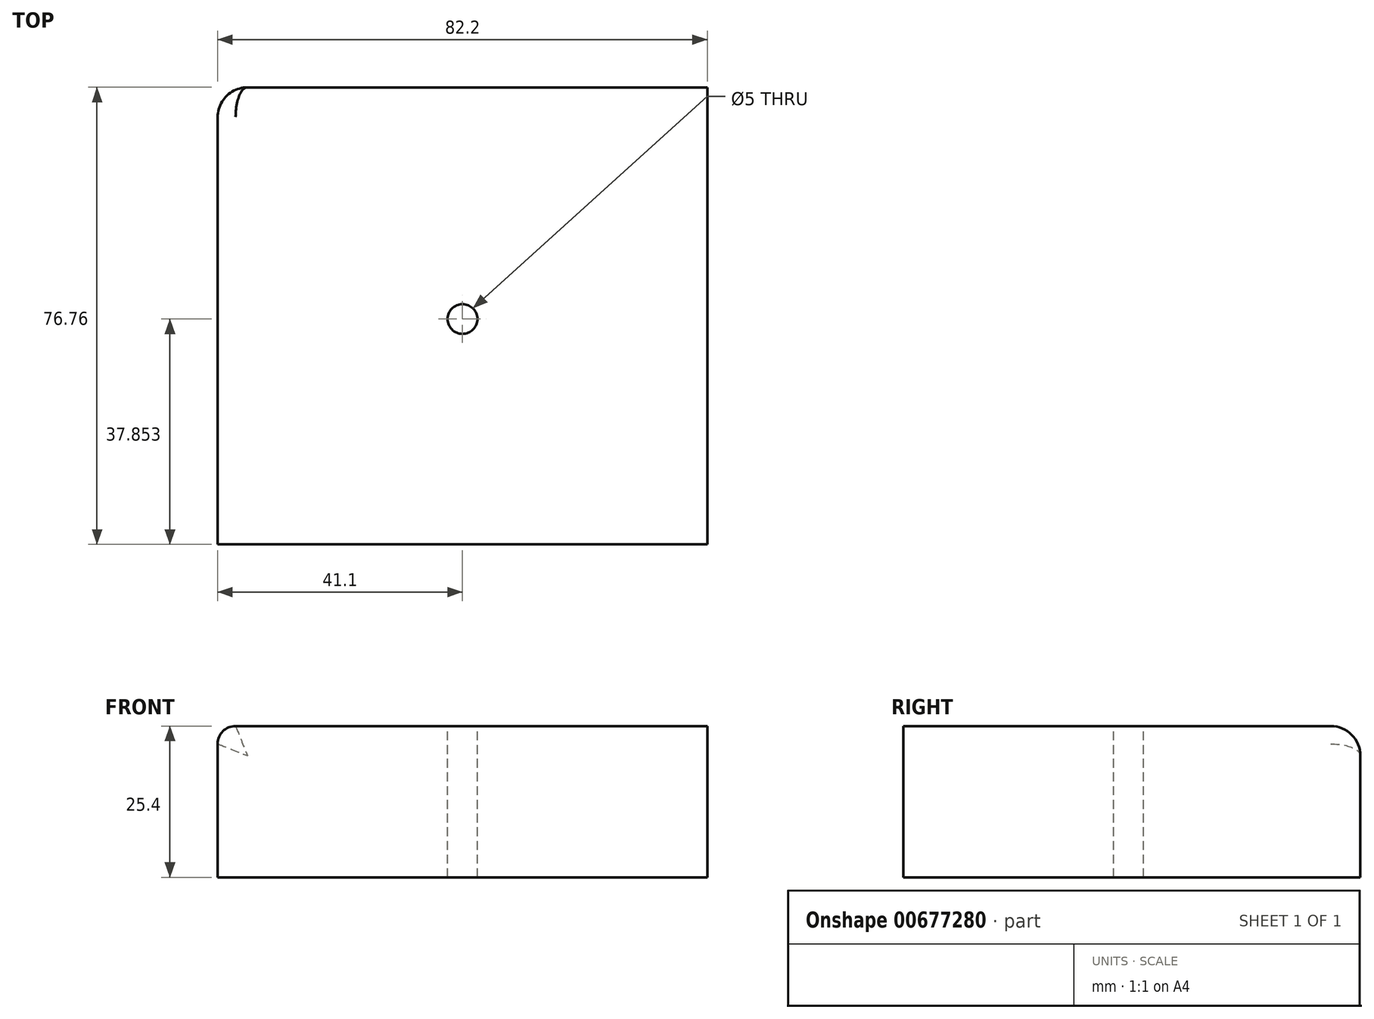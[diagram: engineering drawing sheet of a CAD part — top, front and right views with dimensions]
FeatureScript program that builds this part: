
annotation { "Feature Type Name" : "Feature", "Feature Type Description" : "" }
export const myFeature = defineFeature(function(context is Context, id is Id, definition is map)
    precondition{}
    {
        {
            var Q0;
            Q0=qCreatedBy(makeId("Top.planeOp"),FACE);
            var sketch = newSketch(context, id + "F0", { "sketchPlane" : qUnion([Q0])});
            skLineSegment(sketch, "E0.bottom", {"start": v(41.1, 38.38) * mm, "end": v(-41.1, 38.38) * mm});
            skLineSegment(sketch, "E0.top", {"start": v(41.1, -38.38) * mm, "end": v(-41.1, -38.38) * mm});
            skLineSegment(sketch, "E0.left", {"start": v(41.1, 38.38) * mm, "end": v(41.1, -38.38) * mm});
            skLineSegment(sketch, "E0.right", {"start": v(-41.1, 38.38) * mm, "end": v(-41.1, -38.38) * mm});
            skPoint(sketch, "E0.middle", {"position": v(0, 0) * mm});
            skSolve(sketch);
        }
        {
            var Q0;
            Q0 = qSketchRegion(id + "F0", true);
            extrude(context, id + "F1", {"entities" : qUnion([Q0]), "depth" : 25.4 * mm, "offsetDistance" : 25.4 * mm});
        }
        {
            var Q0;
            Q0=makeQuery(id+"F1.opExtrude","CAP_EDGE",EDGE,{"disambiguationData":[OSD([sQuery(id+"F0.wireOp",EDGE,"E0.right")])],"isStart":false});
            fillet(context, id + "F2", {"entities" : qUnion([Q0]), "radius" : 3 * mm, "tangentPropagation" : true, "allowEdgeOverflow" : false});
        }
        {
            var Q0;
            Q0=makeQuery(id+"F1.opExtrude","CAP_EDGE",EDGE,{"disambiguationData":[OSD([sQuery(id+"F0.wireOp",EDGE,"E0.bottom")])],"isStart":false});
            fillet(context, id + "F3", {"entities" : qUnion([Q0]), "radius" : 5 * mm, "tangentPropagation" : true, "allowEdgeOverflow" : false});
        }
        {
            var Q0;
            Q0=makeQuery(id+"F1.opExtrude","CAP_FACE",FACE,{"disambiguationData":[OSD([sQuery(id+"F0.wireOp",EDGE,"E0.bottom"),sQuery(id+"F0.wireOp",EDGE,"E0.top"),sQuery(id+"F0.wireOp",EDGE,"E0.left"),sQuery(id+"F0.wireOp",EDGE,"E0.right")])],"isStart":false});
            var sketch = newSketch(context, id + "F4", { "sketchPlane" : qUnion([Q0])});
            skPoint(sketch, "E1", {"position": v(0, 17.21) * mm});
            skPoint(sketch, "E2", {"position": v(0, -0.53) * mm});
            skSolve(sketch);
        }
        {
            var Q0;
            Q0=sQuery(id+"F4.wireOp",VERTEX,"E2");
            var Q1;
            Q1=makeQuery(id+"F1.opExtrude","SWEPT_BODY",BODY,{"disambiguationData":[OSD([sQuery(id+"F0.wireOp",EDGE,"E0.bottom"),sQuery(id+"F0.wireOp",EDGE,"E0.top"),sQuery(id+"F0.wireOp",EDGE,"E0.left"),sQuery(id+"F0.wireOp",EDGE,"E0.right")])]});
            hole(context, id + "F5", {"style" : HoleStyle.SIMPLE, "endStyle" : HoleEndStyle.THROUGH, "holeDiameter" : 5 * mm, "majorDiameter" : 5 * mm, "isTappedThrough" : true, "tappedDepth" : 12 * mm, "tapClearance" : 3, "locations" : qUnion([Q0]), "scope" : qUnion([Q1])});
        }
    });
